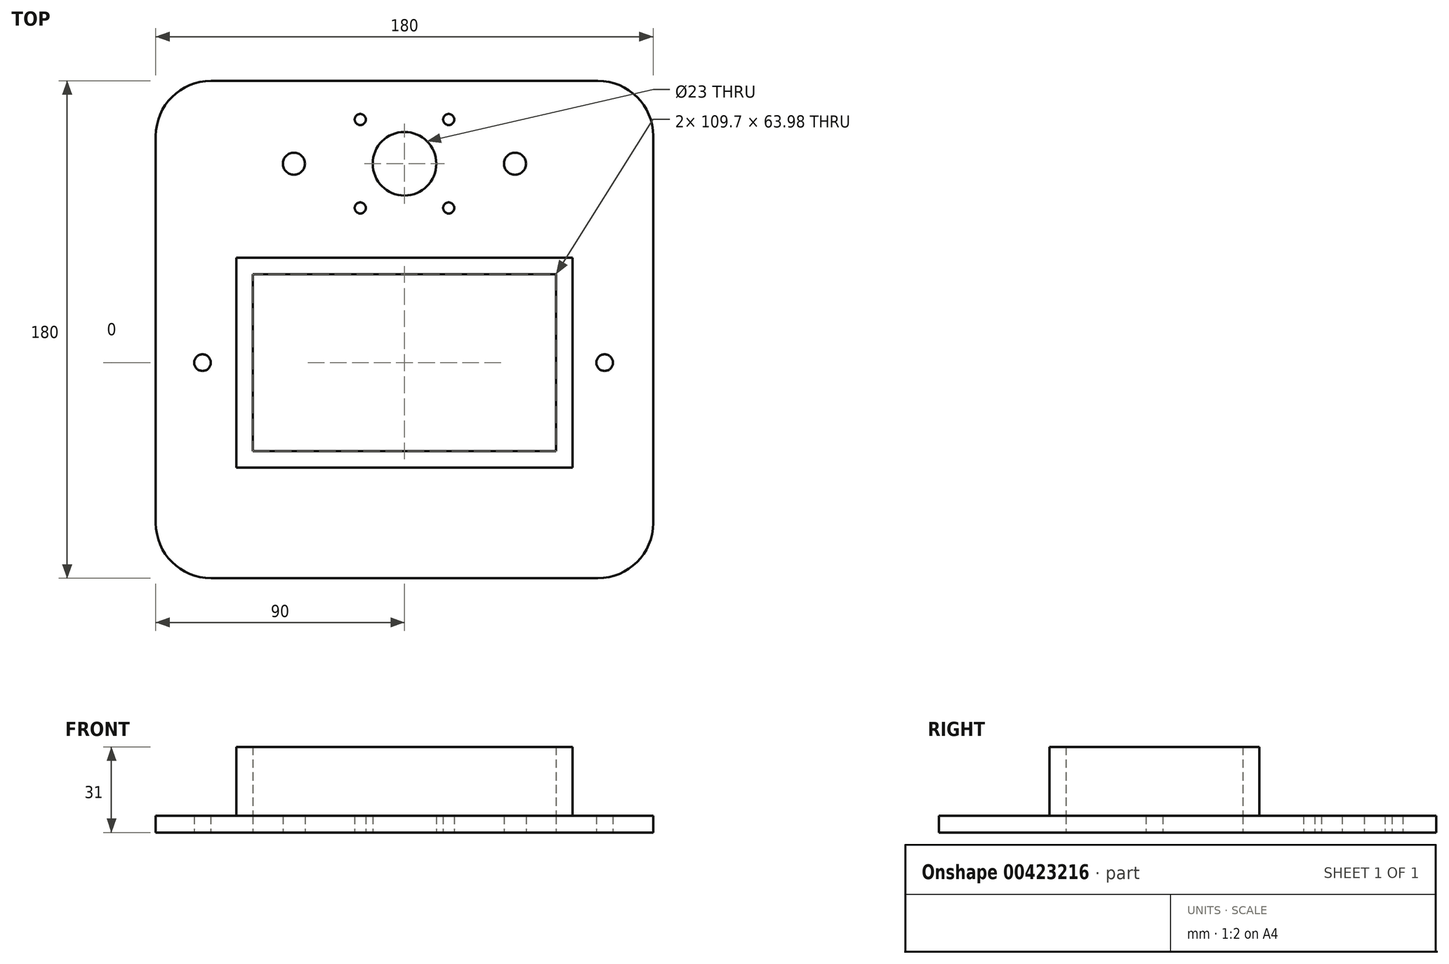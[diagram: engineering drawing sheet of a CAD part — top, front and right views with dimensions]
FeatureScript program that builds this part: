
annotation { "Feature Type Name" : "Feature", "Feature Type Description" : "" }
export const myFeature = defineFeature(function(context is Context, id is Id, definition is map)
    precondition{}
    {
        {
            var Q0;
            Q0=qCreatedBy(makeId("Top.planeOp"),FACE);
            var sketch = newSketch(context, id + "F0", { "sketchPlane" : qUnion([Q0])});
            skLineSegment(sketch, "E0.bottom", {"start": v(-54.85, 0) * mm, "end": v(54.85, 0) * mm});
            skLineSegment(sketch, "E0.top", {"start": v(-54.85, -63.98) * mm, "end": v(54.85, -63.98) * mm});
            skLineSegment(sketch, "E0.left", {"start": v(54.85, 0) * mm, "end": v(54.85, -63.98) * mm});
            skLineSegment(sketch, "E0.right", {"start": v(-54.85, 0) * mm, "end": v(-54.85, -63.98) * mm});
            skCircle(sketch, "E1", {"center": v(-40, 40) * mm, "radius": 4 * mm});
            skCircle(sketch, "E2", {"center": v(40, 40) * mm, "radius": 4 * mm});
            skCircle(sketch, "E3", {"center": v(0, 40) * mm, "radius": 11.5 * mm});
            skLineSegment(sketch, "E4.bottom", {"start": v(-70, 70) * mm, "end": v(70, 70) * mm});
            skLineSegment(sketch, "E4.top", {"start": v(-70, -110) * mm, "end": v(70, -110) * mm});
            skLineSegment(sketch, "E4.left", {"start": v(-90, 50) * mm, "end": v(-90, -90) * mm});
            skLineSegment(sketch, "E4.right", {"start": v(90, 50) * mm, "end": v(90, -90) * mm});
            skPoint(sketch, "E5.visualSharp", {"position": v(-90, 70) * mm});
            skArc(sketch, "E5.filletArc", {"start": v(-70, 70) * mm, "mid": v(-84.14, 64.14) * mm, "end": v(-90, 50) * mm});
            skPoint(sketch, "E6.visualSharp", {"position": v(90, 70) * mm});
            skArc(sketch, "E6.filletArc", {"start": v(90, 50) * mm, "mid": v(84.14, 64.14) * mm, "end": v(70, 70) * mm});
            skPoint(sketch, "E7.visualSharp", {"position": v(90, -110) * mm});
            skArc(sketch, "E7.filletArc", {"start": v(70, -110) * mm, "mid": v(84.14, -104.14) * mm, "end": v(90, -90) * mm});
            skPoint(sketch, "E8.visualSharp", {"position": v(-90, -110) * mm});
            skArc(sketch, "E8.filletArc", {"start": v(-90, -90) * mm, "mid": v(-84.14, -104.14) * mm, "end": v(-70, -110) * mm});
            skPoint(sketch, "E9", {"position": v(-90, -32) * mm});
            skPoint(sketch, "E9.positionSnap0", {"position": v(-54.85, -32) * mm});
            skPoint(sketch, "E10", {"position": v(54.85, -32) * mm});
            skPoint(sketch, "E11", {"position": v(90, -32) * mm});
            skCircle(sketch, "E12", {"center": v(-73.09, -32) * mm, "radius": 3 * mm});
            skCircle(sketch, "E13", {"center": v(72.43, -32) * mm, "radius": 3 * mm});
            skPoint(sketch, "E14", {"position": v(0, 70) * mm});
            skPoint(sketch, "E15", {"position": v(0, -110) * mm});
            skLineSegment(sketch, "E16.bottom", {"start": v(16, 24) * mm, "end": v(-16, 24) * mm, "construction": true});
            skLineSegment(sketch, "E16.top", {"start": v(16, 56) * mm, "end": v(-16, 56) * mm, "construction": true});
            skLineSegment(sketch, "E16.left", {"start": v(16, 24) * mm, "end": v(16, 56) * mm, "construction": true});
            skLineSegment(sketch, "E16.right", {"start": v(-16, 24) * mm, "end": v(-16, 56) * mm, "construction": true});
            skCircle(sketch, "E17", {"center": v(-16, 56) * mm, "radius": 2 * mm});
            skCircle(sketch, "E18", {"center": v(16, 56) * mm, "radius": 2 * mm});
            skCircle(sketch, "E19", {"center": v(16, 24) * mm, "radius": 2 * mm});
            skCircle(sketch, "E20", {"center": v(-16, 24) * mm, "radius": 2 * mm});
            skSolve(sketch);
        }
        {
            var Q0;
            Q0=makeQuery(id+"F0.imprint","IMPRINT",FACE,{"disambiguationData":[TD([[makeQuery(id+"F0.imprint","IMPRINT",EDGE,{"derivedFrom":sQuery(id+"F0.wireOp",EDGE,"E0.bottom")}),1.0]])]});
            extrude(context, id + "F1", {"entities" : qUnion([Q0]), "depth" : 6 * mm});
        }
        {
            var Q0;
            Q0=makeQuery(id+"F1.opExtrude","CAP_FACE",FACE,{"disambiguationData":[OSD([sQuery(id+"F0.wireOp",EDGE,"E0.bottom"),sQuery(id+"F0.wireOp",EDGE,"E0.top"),sQuery(id+"F0.wireOp",EDGE,"E0.left"),sQuery(id+"F0.wireOp",EDGE,"E0.right"),sQuery(id+"F0.wireOp",EDGE,"E1"),sQuery(id+"F0.wireOp",EDGE,"E2"),sQuery(id+"F0.wireOp",EDGE,"E3"),sQuery(id+"F0.wireOp",EDGE,"E4.bottom"),sQuery(id+"F0.wireOp",EDGE,"E4.top"),sQuery(id+"F0.wireOp",EDGE,"E4.left"),sQuery(id+"F0.wireOp",EDGE,"E4.right"),sQuery(id+"F0.wireOp",EDGE,"E5.filletArc"),sQuery(id+"F0.wireOp",EDGE,"E6.filletArc"),sQuery(id+"F0.wireOp",EDGE,"E7.filletArc"),sQuery(id+"F0.wireOp",EDGE,"E8.filletArc"),sQuery(id+"F0.wireOp",EDGE,"E12"),sQuery(id+"F0.wireOp",EDGE,"E13")])],"isStart":false});
            var sketch = newSketch(context, id + "F2", { "sketchPlane" : qUnion([Q0])});
            skLineSegment(sketch, "E21.0", {"start": v(-60.85, 6) * mm, "end": v(60.85, 6) * mm});
            skLineSegment(sketch, "E21.1", {"start": v(-60.85, 6) * mm, "end": v(-60.85, -69.98) * mm});
            skLineSegment(sketch, "E21.2", {"start": v(-60.85, -69.98) * mm, "end": v(60.85, -69.98) * mm});
            skLineSegment(sketch, "E21.3", {"start": v(60.85, 6) * mm, "end": v(60.85, -69.98) * mm});
            skLineSegment(sketch, "E22.0", {"start": v(-54.85, -63.98) * mm, "end": v(54.85, -63.98) * mm});
            skLineSegment(sketch, "E22.1", {"start": v(-54.85, 0) * mm, "end": v(-54.85, -63.98) * mm});
            skLineSegment(sketch, "E22.2", {"start": v(-54.85, 0) * mm, "end": v(54.85, 0) * mm});
            skLineSegment(sketch, "E22.3", {"start": v(54.85, 0) * mm, "end": v(54.85, -63.98) * mm});
            skSolve(sketch);
        }
        {
            var Q0;
            Q0=makeQuery(id+"F2.imprint","IMPRINT",FACE,{"disambiguationData":[TD([[makeQuery(id+"F2.imprint","IMPRINT",EDGE,{"derivedFrom":sQuery(id+"F2.wireOp",EDGE,"E21.0")}),-1.0]])]});
            extrude(context, id + "F3", {"entities" : qUnion([Q0]), "depth" : 25 * mm});
        }
    });
